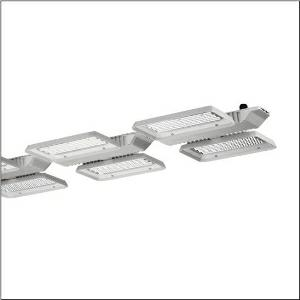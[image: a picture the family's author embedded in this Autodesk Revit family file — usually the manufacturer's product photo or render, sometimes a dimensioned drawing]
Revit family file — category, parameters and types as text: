
# Revit family: highbay_11_51hla1d34sca
name_source: partatom
category: Lighting Fixtures
units: mm (PartAtom-declared; Revit-internal decimal feet)

## family parameters
Cut with Voids When Loaded = No
Host = Face
Light Source = No
Part Type = Normal
Room Calculation Point = No
Round Connector Dimension = Use Diameter
Shared = No

## types (1)
- --- (1 x LED, 48560 lm, 284.4 W, 4000K)
    Apparent Load = 284 VA
    CIE Flux Codes = 88 95 99 100 99
    Color Rendering = 80
    Color Temperature = 4000K
    Default Elevation = 1800 mm
    Description = Highbay 11, LED high bay luminaire, primary light control with lens, of PMMA, light emission: direct distribution, primary light characteristic: symmetric, installation type: surface-mounted, suspended mounting, for 3x 2 x LED rated luminous flux: 48.560 lm, light colour: 840, colour temperature: 4000K, control gear: ECG DALI, with terminal, 5-pole, max. 2.5mm², mains connection: 230..240V, AC, 50/60Hz, rated input power: 284W, LED unit, of diecast aluminium, unplated, bead blasted, silver, length: 1.410 mm, width: 500 mm, height: 65mm, housing, of diecast aluminium, uncoated, bead blasted, silver, protection rating (complete): IP65, insulation class (complete): insulation class I (protective earthing), certification: CE, ENEC, VDE, protection symbol: D, impact resistance: IK08 with glass or PC cover, permissible ambient temperature for indoor applications: -35..+45°C, reducing of maximum allowable ambient temperature of 5°C with ceiling mounting, corresponds to IFS (International Featured Standards) requirements for safety and quality in the food industry, packaging unit: 1 piece
    Height = 95 mm
    Lamp = 1 x LED
    Lamp Light Flux = 48560 lm
    Lamp Power = 284.4 W
    Lamp count = 1
    Length = 1410 mm
    Luminous efficacy = 171 lm/W
    Manufacturer = Siteco
    ModVariant = No
    Model = 51HLA1D34SCA
    Mounting Place = Ceiling
    Mounting Type = Pendant
    Number of Poles = 1
    OnlyDefault = Yes
    Power Factor = 1
    Product Name = Highbay 11
    Product group = LED high bay luminaire
    ProductGroupID = 903
    Protection Class = Protection class I
    Protection Degree = IP 65
    RLX_Detail_Level = 1
    RlxData = <blob elided: 105101 chars, md5=025cd6b2>
    Socket = socket
    Standby Power = 0 W
    System Light Flux = 48560 lm
    System Power = 284 W
    Type Comments = factory setting: luminous flux: 100 % | dim-lin: 254 | 535 mA
    Type Image = l_1003314.jpg
    URL = http://relux.com
    VarID = @adj_141049
    Voltage = 0 V
    Weight = 0.00 kg
    Width = 501 mm

## geometry (parser evidence)
native form markers: Blend x4, Sweep x13
no freeform markers — native parametric forms only
